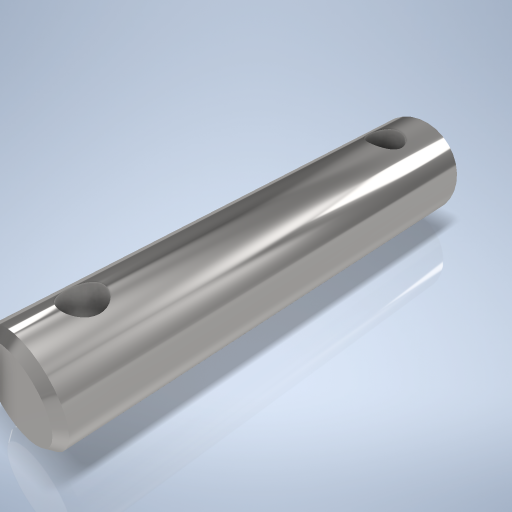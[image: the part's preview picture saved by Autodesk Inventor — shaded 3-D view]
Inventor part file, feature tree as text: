
AUTODESK INVENTOR PART (.ipt)
format: ipt  version: 2024.2 (Build 282272000, 272)  size: 308,224 bytes
history: native  units: mm
features: sketch x2, extrude x1, chamfer x1, plane x1, hole x1
ambient origin geometry x8: Origin, YZ Plane, XZ Plane, XY Plane, X Axis, Y Axis, Z Axis, Center Point
bodies: Volumenkörper1 (feature_tree)
feature tree (6):
  extrude  "Extrusion1"  Depth=30.0mm TaperAngle=0.0deg
  chamfer  "Fasen1"  Distance=0.5mm Angle=45.0deg
  plane  "Arbeitsebene4"
  hole  "Bohrung3"  [1 undecoded]
  sketch  "Skizze1"  dims[d0=6.5mm d1=30.0mm d2=0.0mm d3=0.5mm d4=2.0mm d5=45.0deg]
  sketch  "Skizze4"  dims[d24=3.25mm d25=4.0mm d26=4.0mm d27=2.5mm d28=6.0mm d29=4.0mm d30=2.0mm d31=90.0deg d32=8.0mm d33=20.594885mm]
note: 1 required parameter value undecoded (feature->parameter linkage not recoverable at this tier; creation-order binding heuristic only, values carry confidence <= 0.55)
